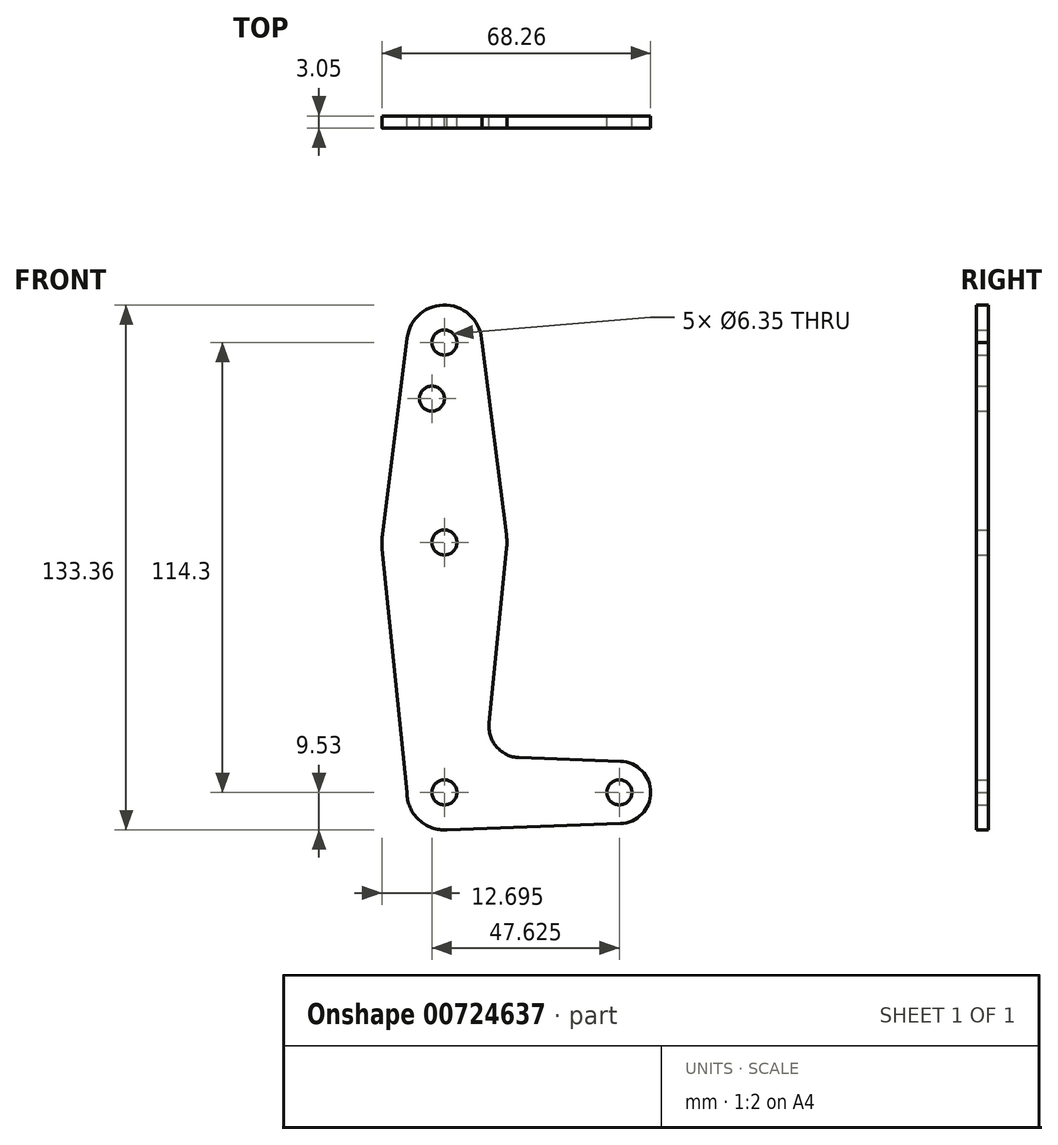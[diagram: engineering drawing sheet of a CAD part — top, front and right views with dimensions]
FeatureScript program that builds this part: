
annotation { "Feature Type Name" : "Feature", "Feature Type Description" : "" }
export const myFeature = defineFeature(function(context is Context, id is Id, definition is map)
    precondition{}
    {
        {
            var Q0;
            Q0=qCreatedBy(makeId("Front.planeOp"),FACE);
            var sketch = newSketch(context, id + "F0", { "sketchPlane" : qUnion([Q0])});
            skLineSegment(sketch, "E0", {"start": v(0, 0) * mm, "end": v(0, 114.3) * mm});
            skLineSegment(sketch, "E1", {"start": v(0, 0) * mm, "end": v(44.45, 0) * mm});
            skCircle(sketch, "E2", {"center": v(0, 114.3) * mm, "radius": 9.53 * mm});
            skCircle(sketch, "E3", {"center": v(0, 0) * mm, "radius": 9.53 * mm});
            skCircle(sketch, "E4", {"center": v(44.45, 0) * mm, "radius": 7.94 * mm});
            skCircle(sketch, "E5", {"center": v(0, 63.5) * mm, "radius": 15.88 * mm});
            skLineSegment(sketch, "E6", {"start": v(-9.45, 115.5) * mm, "end": v(-15.75, 65.48) * mm});
            skLineSegment(sketch, "E7", {"start": v(18.97, 8.85) * mm, "end": v(44.73, 7.93) * mm});
            skLineSegment(sketch, "E8", {"start": v(0, -9.53) * mm, "end": v(44.73, -7.93) * mm});
            skCircle(sketch, "E9", {"center": v(0, 114.3) * mm, "radius": 3.18 * mm});
            skLineSegment(sketch, "E10", {"start": v(9.53, 114.3) * mm, "end": v(15.75, 65.5) * mm});
            skLineSegment(sketch, "E11", {"start": v(-9.52, 0) * mm, "end": v(-15.8, 61.9) * mm});
            skCircle(sketch, "E12", {"center": v(0, 63.5) * mm, "radius": 3.18 * mm});
            skCircle(sketch, "E13", {"center": v(44.45, 0) * mm, "radius": 3.18 * mm});
            skCircle(sketch, "E14", {"center": v(0, 0) * mm, "radius": 3.18 * mm});
            skLineSegment(sketch, "E15", {"start": v(15.8, 61.91) * mm, "end": v(11.34, 17.59) * mm});
            skPoint(sketch, "E16.newPointB", {"position": v(0, 9.53) * mm});
            skArc(sketch, "E16.filletArc", {"start": v(11.34, 17.59) * mm, "mid": v(12.54, 12.53) * mm, "end": v(16.62, 9.3) * mm});
            skArc(sketch, "E17.filletArc", {"start": v(16.62, 9.3) * mm, "mid": v(17.78, 8.98) * mm, "end": v(18.97, 8.85) * mm});
            skCircle(sketch, "E18", {"center": v(-3.18, 100.03) * mm, "radius": 3.18 * mm});
            skSolve(sketch);
        }
        {
            var Q0;
            Q0 = qSketchRegion(id + "F0", true);
            var Q1;
            {var subQ0=sQuery(id+"F0.wireOp",EDGE,"E14");var subQ1=sQuery(id+"F0.wireOp",EDGE,"E0");var subQ2=makeQuery(id+"F0.imprint","INTERSECT",VERTEX,{"derivedFrom":[subQ1,subQ0]});Q1=makeQuery(id+"F0.imprint","IMPRINT",FACE,{"disambiguationData":[TD([[makeQuery(id+"F0.imprint","IMPRINT",EDGE,{"disambiguationData":[TD([[subQ2,-1.0]])],"derivedFrom":subQ1}),-1.0]])]});}
            extrude(context, id + "F1", {"entities" : qUnion([Q0, Q1]), "depth" : 3.05 * mm, "offsetDistance" : 25.4 * mm});
        }
    });
